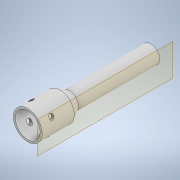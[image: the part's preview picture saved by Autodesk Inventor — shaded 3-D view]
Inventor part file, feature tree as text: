
AUTODESK INVENTOR PART (.ipt)
format: ipt  version: 2021 (Build 250183000, 183)  size: 147,456 bytes
history: native  units: in
note: dims shown in document units (in); Inventor stores cm internally (conversion verified against a paired STEP export)
features: sketch x2, revolve x1, plane x1, extrude x1, pattern_circular x1
ambient origin geometry x8: Origin, YZ Plane, XZ Plane, XY Plane, X Axis, Y Axis, Z Axis, Center Point
bodies: Solid1 (feature_tree)
feature tree (6):
  revolve  "Revolution1"  [1 undecoded]
  plane  "Work Plane2"
  extrude  "Extrusion1"  Depth=0.0354in
  pattern_circular  "Circular Pattern1"  [2 undecoded]
  sketch  "Sketch1"  dims[d7=0.2165in d8=0.1181in]
  sketch  "Sketch2"  dims[d9=150.0deg d10=0.0354in d11=0.0354in d12=0.0354in d13=0.5512in d14=1.4252in d15=90.0deg d17=0.2756in d18=0.1969in d19=0.1339in d20=0.0787in d21=0.1969in d22=0.0in d28=1.5748in d29=360.0deg]
note: 3 required parameter values undecoded (feature->parameter linkage not recoverable at this tier; creation-order binding heuristic only, values carry confidence <= 0.55)